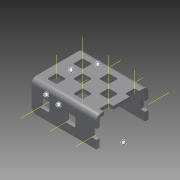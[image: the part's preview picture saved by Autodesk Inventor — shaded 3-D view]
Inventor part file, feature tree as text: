
AUTODESK INVENTOR PART (.ipt)
format: ipt  version: 2015 (Build 190159000, 159)  size: 1,915,392 bytes
history: native  units: in
note: dims shown in document units (in); Inventor stores cm internally (conversion verified against a paired STEP export)
features: other x21, pattern_linear x3, sheet_metal_op x1, extrude x1, imported_body x1, sketch x1
ambient origin geometry x8: Origin, YZ Plane, XZ Plane, XY Plane, X Axis, Y Axis, Z Axis, Center Point
bodies: Body1 (feature_tree)
feature tree (28):
  sheet_metal_op  "Fold1"
  other  "C-Channel"
  extrude  "length cut"  Depth=0.5in
  other  "top axis"
  other  "inner axis"
  other  "front axis"
  other  "back axis"
  pattern_linear  "top axes"  Spacing1=0.5in  [1 undecoded]
  pattern_linear  "inner axes"  Spacing1=0.5in  [1 undecoded]
  pattern_linear  "horiz axes"  Spacing1=-1.25in  [1 undecoded]
  other  "right plane"
  imported_body  "Base1"
  sketch  "Sketch1"  dims[d1=0.0in d4=0.5in d5=0.7874in d7=0.5in d10=0.5in d13=0.5in d14=-1.25in d15=0.0in d16=0.0in d17=0.0in d18=0.0in d19=0.0in]
  other  "Work Point1"
  other  "Work Point2"
  other  "Work Point3"
  other  "Work Point4"
  other  "Work Axis5"
  other  "Work Axis6"
  other  "Work Axis11"
  other  "Work Axis12"
  other  "Work Axis13"
  other  "Work Axis18"
  other  "Work Axis23"
  other  "Work Axis24"
  other  "Work Axis30"
  other  "Work Axis31"
  other  "left plane"
note: 3 required parameter values undecoded (feature->parameter linkage not recoverable at this tier; creation-order binding heuristic only, values carry confidence <= 0.55)
